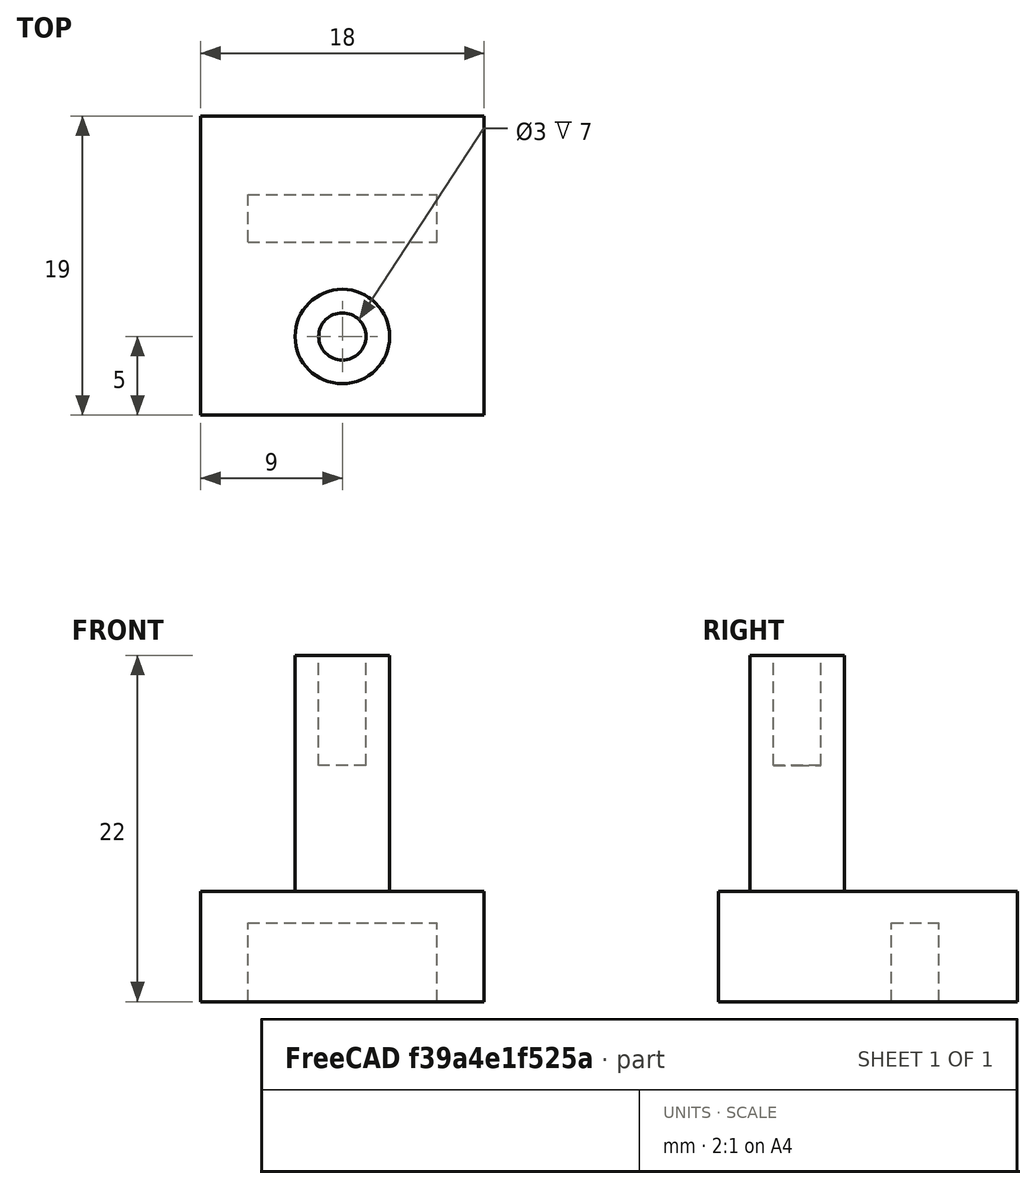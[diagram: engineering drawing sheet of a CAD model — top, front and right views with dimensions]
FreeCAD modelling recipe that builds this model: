
FCSTD DOCUMENT  (FreeCAD 0.17R13541 (Git))
Label: cam mt raise
License: All rights reserved
LicenseURL: http://en.wikipedia.org/wiki/All_rights_reserved
objects: Part::Cylinder×2, Part::Box×2, Part::Cut×2
note: 6 computed .brp shape members not serialized (recipe doc carries the construction recipe); baked Part::Feature solids carry a one-line shape summary decoded from their .brp

FEATURE [Part::Cylinder] Cylinder
  Angle = 360
  AttacherType = Attacher::AttachEngine3D
  Height = 15
  Radius = 3
FEATURE [Part::Cylinder] Cylinder001
  Angle = 360
  AttacherType = Attacher::AttachEngine3D
  Height = 7
  Placement = pos=(0,0,8) rot=(0,0,1;0rad)
  Radius = 1.5
FEATURE [Part::Box] Box  label="Cube"
  AttacherType = Attacher::AttachEngine3D
  Height = 7
  Length = 18
  Width = 19
FEATURE [Part::Box] Box001  label="Cube001"
  AttacherType = Attacher::AttachEngine3D
  Height = 5
  Length = 12
  Placement = pos=(3,11,0) rot=(0,0,1;0rad)
  Width = 3
FEATURE [Part::Cut] Cut
  Base = -> Cylinder
  Placement = pos=(9,5,7) rot=(0,0,1;0rad)
  Tool = -> Cylinder001
FEATURE [Part::Cut] Cut001
  Base = -> Box
  Tool = -> Box001
